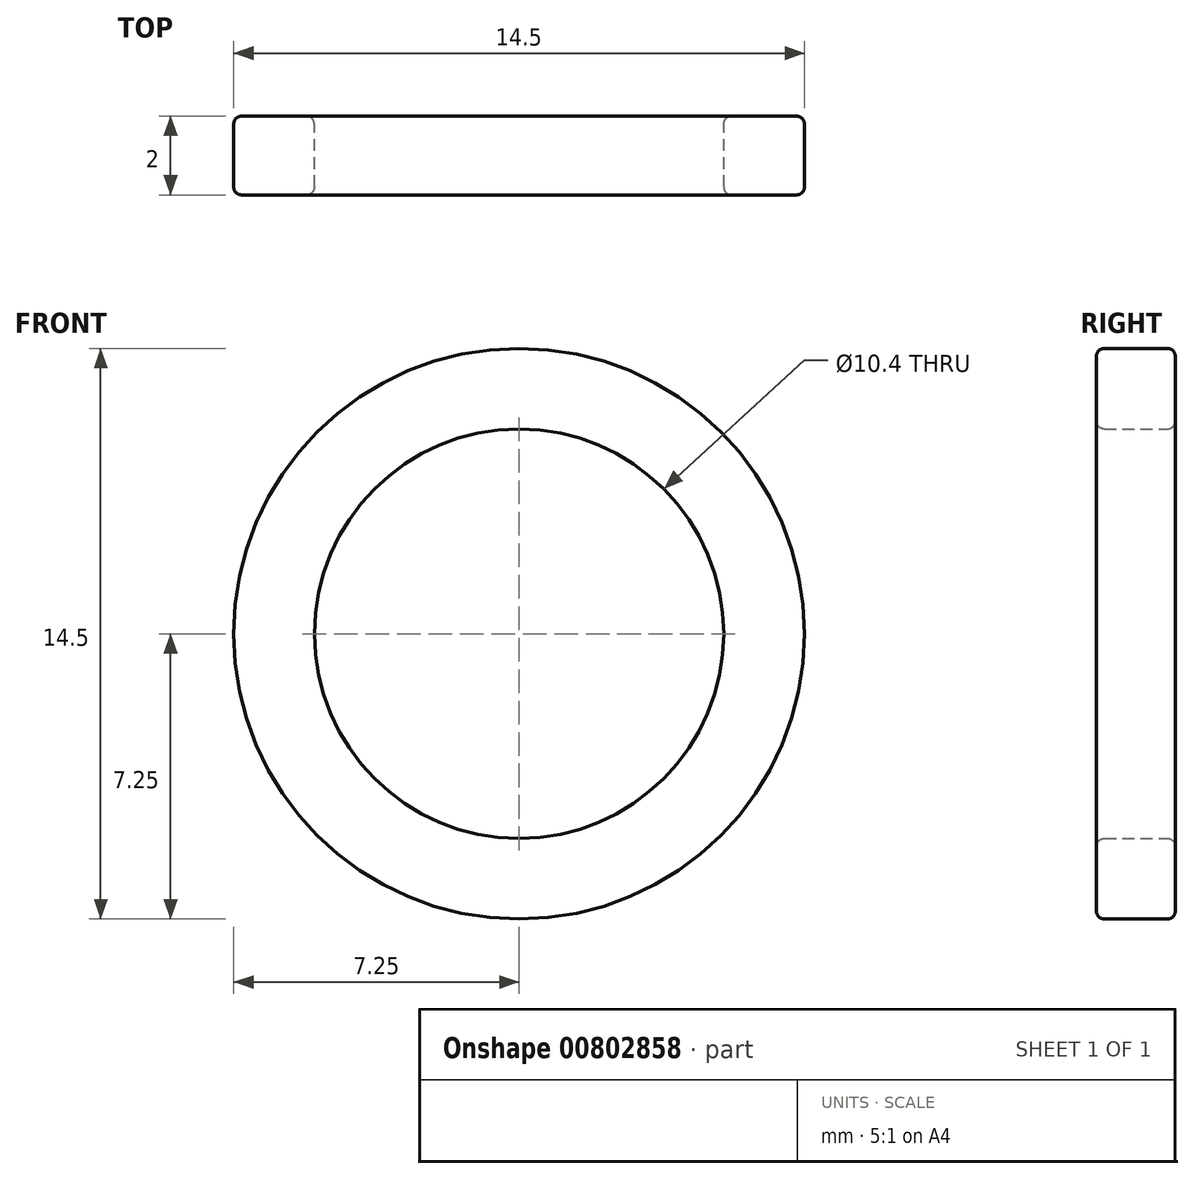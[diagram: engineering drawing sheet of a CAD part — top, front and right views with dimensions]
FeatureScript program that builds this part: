
annotation { "Feature Type Name" : "Feature", "Feature Type Description" : "" }
export const myFeature = defineFeature(function(context is Context, id is Id, definition is map)
    precondition{}
    {
        {
            var Q0;
            Q0=qCreatedBy(makeId("Front.planeOp"),FACE);
            var sketch = newSketch(context, id + "F0", { "sketchPlane" : qUnion([Q0])});
            skCircle(sketch, "E0", {"center": v(0, 0) * mm, "radius": 5.2 * mm});
            skCircle(sketch, "E1", {"center": v(0, 0) * mm, "radius": 7.25 * mm});
            skSolve(sketch);
        }
        {
            var Q0;
            Q0=qSketchRegion(id+"F0",true);
            extrude(context, id + "F1", {"entities" : qUnion([Q0]), "depth" : 2 * mm, "offsetDistance" : 25 * mm});
        }
        {
            var Q0;
            Q0=makeQuery(id+"F1.opExtrude","CAP_FACE",FACE,{"disambiguationData":[OSD([sQuery(id+"F0.wireOp",EDGE,"E0"),sQuery(id+"F0.wireOp",EDGE,"E1")])],"isStart":false});
            var Q1;
            Q1=makeQuery(id+"F1.opExtrude","CAP_FACE",FACE,{"disambiguationData":[OSD([sQuery(id+"F0.wireOp",EDGE,"E0"),sQuery(id+"F0.wireOp",EDGE,"E1")])],"isStart":true});
            fillet(context, id + "F2", {"entities" : qUnion([Q0, Q1]), "radius" : 0.2 * mm, "tangentPropagation" : true, "allowEdgeOverflow" : false});
        }
    });
